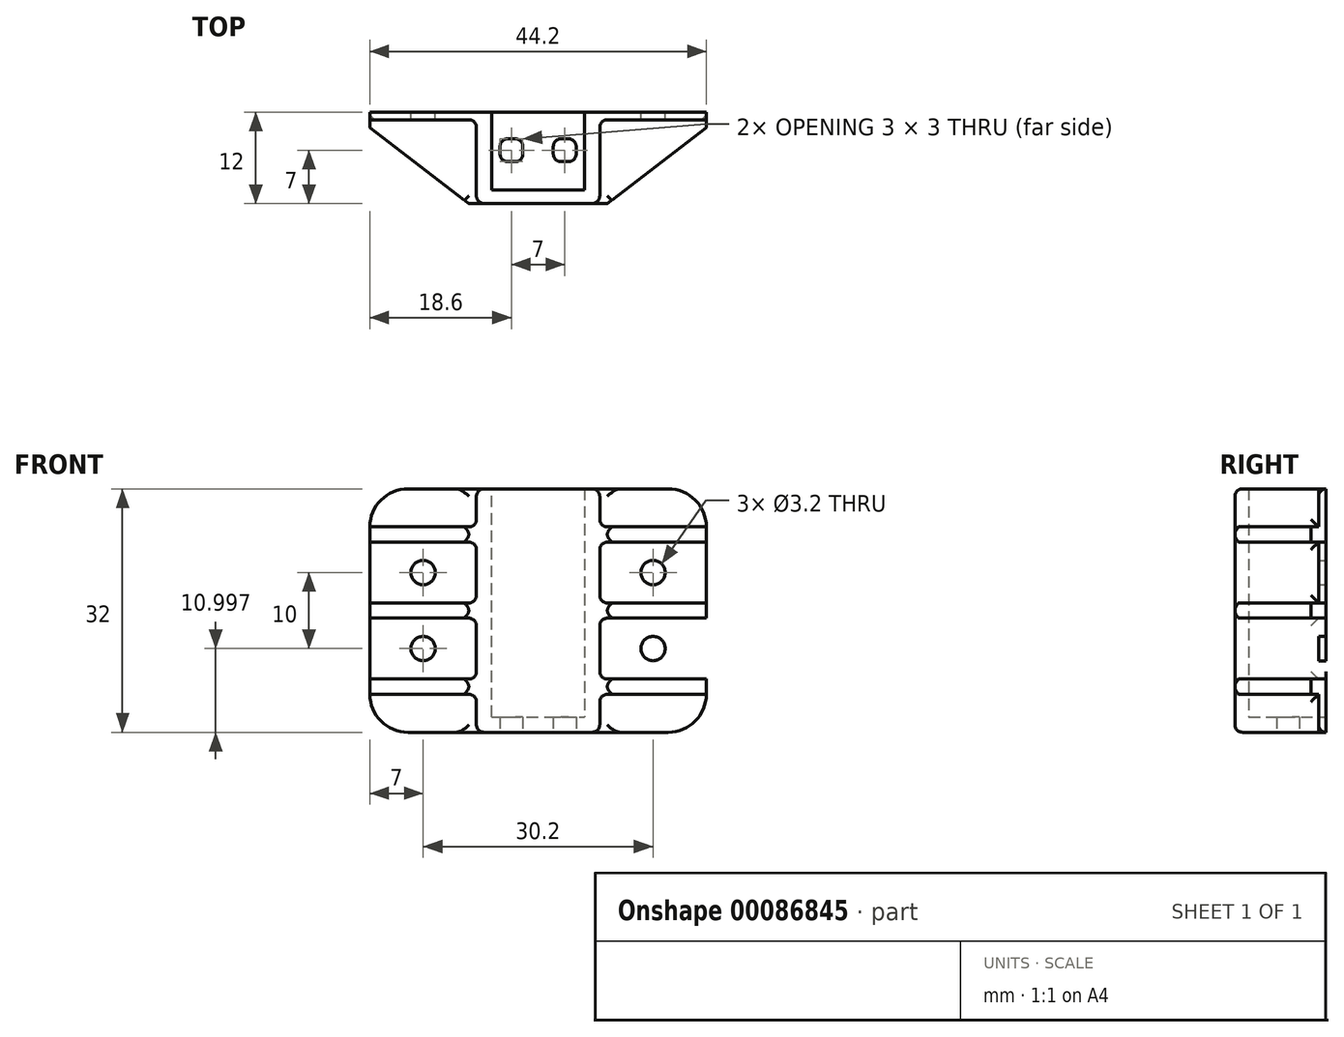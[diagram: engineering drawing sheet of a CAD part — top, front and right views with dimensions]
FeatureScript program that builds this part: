
annotation { "Feature Type Name" : "Feature", "Feature Type Description" : "" }
export const myFeature = defineFeature(function(context is Context, id is Id, definition is map)
    precondition{}
    {
        {
            var Q0;
            Q0=qCreatedBy(makeId("Front.planeOp"),FACE);
            var sketch = newSketch(context, id + "F0", { "sketchPlane" : qUnion([Q0])});
            skLineSegment(sketch, "E0.bottom", {"start": v(-6.1, 29.45) * mm, "end": v(6.1, 29.45) * mm});
            skLineSegment(sketch, "E0.top", {"start": v(-6.1, -0.55) * mm, "end": v(6.1, -0.55) * mm});
            skLineSegment(sketch, "E0.left", {"start": v(-6.1, 29.45) * mm, "end": v(-6.1, -0.55) * mm});
            skLineSegment(sketch, "E0.right", {"start": v(6.1, 29.45) * mm, "end": v(6.1, -0.55) * mm});
            skLineSegment(sketch, "E1.bottom", {"start": v(-22.1, 29.45) * mm, "end": v(22.1, 29.45) * mm});
            skLineSegment(sketch, "E1.top", {"start": v(-22.1, -2.55) * mm, "end": v(22.1, -2.55) * mm});
            skLineSegment(sketch, "E1.left", {"start": v(-22.1, 29.45) * mm, "end": v(-22.1, -2.55) * mm});
            skLineSegment(sketch, "E1.right", {"start": v(22.1, 29.45) * mm, "end": v(22.1, -2.55) * mm});
            skLineSegment(sketch, "E2.bottom", {"start": v(-8.1, 29.45) * mm, "end": v(8.1, 29.45) * mm});
            skLineSegment(sketch, "E2.top", {"start": v(-8.1, -2.55) * mm, "end": v(8.1, -2.55) * mm});
            skLineSegment(sketch, "E2.left", {"start": v(-8.1, 29.45) * mm, "end": v(-8.1, -2.55) * mm});
            skLineSegment(sketch, "E2.right", {"start": v(8.1, 29.45) * mm, "end": v(8.1, -2.55) * mm});
            skLineSegment(sketch, "E3.bottom", {"start": v(-8.1, 24.45) * mm, "end": v(-22.1, 24.45) * mm});
            skLineSegment(sketch, "E3.top", {"start": v(-8.1, 22.45) * mm, "end": v(-22.1, 22.45) * mm});
            skLineSegment(sketch, "E3.left", {"start": v(-8.1, 24.45) * mm, "end": v(-8.1, 22.45) * mm});
            skLineSegment(sketch, "E3.right", {"start": v(-22.1, 24.45) * mm, "end": v(-22.1, 22.45) * mm});
            skLineSegment(sketch, "E4.bottom", {"start": v(-8.1, 14.45) * mm, "end": v(-22.1, 14.45) * mm});
            skLineSegment(sketch, "E4.top", {"start": v(-8.1, 12.45) * mm, "end": v(-22.1, 12.45) * mm});
            skLineSegment(sketch, "E4.left", {"start": v(-8.1, 14.45) * mm, "end": v(-8.1, 12.45) * mm});
            skLineSegment(sketch, "E4.right", {"start": v(-22.1, 14.45) * mm, "end": v(-22.1, 12.45) * mm});
            skLineSegment(sketch, "E5.bottom", {"start": v(-8.1, 4.45) * mm, "end": v(-22.1, 4.45) * mm});
            skLineSegment(sketch, "E5.top", {"start": v(-8.1, 2.45) * mm, "end": v(-22.1, 2.45) * mm});
            skLineSegment(sketch, "E5.left", {"start": v(-8.1, 4.45) * mm, "end": v(-8.1, 2.45) * mm});
            skLineSegment(sketch, "E5.right", {"start": v(-22.1, 4.45) * mm, "end": v(-22.1, 2.45) * mm});
            skPoint(sketch, "E6", {"position": v(-15.1, 18.45) * mm});
            skPoint(sketch, "E6.positionSnap0", {"position": v(-15.1, 22.45) * mm});
            skPoint(sketch, "E7", {"position": v(-15.1, 8.45) * mm});
            skCircle(sketch, "E8", {"center": v(-15.1, 18.45) * mm, "radius": 1.6 * mm});
            skCircle(sketch, "E9", {"center": v(-15.1, 8.45) * mm, "radius": 1.6 * mm});
            skLineSegment(sketch, "E10.MirrorCS", {"start": v(22.1, 24.45) * mm, "end": v(22.1, 22.45) * mm});
            skLineSegment(sketch, "E11.MirrorCS", {"start": v(8.1, 14.45) * mm, "end": v(8.1, 12.45) * mm});
            skLineSegment(sketch, "E12.MirrorCS", {"start": v(8.1, 4.45) * mm, "end": v(8.1, 2.45) * mm});
            skLineSegment(sketch, "E13.MirrorCS", {"start": v(22.1, 4.45) * mm, "end": v(22.1, 2.45) * mm});
            skLineSegment(sketch, "E14.MirrorCS", {"start": v(22.1, 14.45) * mm, "end": v(22.1, 12.45) * mm});
            skLineSegment(sketch, "E15.MirrorCS", {"start": v(8.1, 24.45) * mm, "end": v(8.1, 22.45) * mm});
            skLineSegment(sketch, "E16.MirrorCS", {"start": v(8.1, 14.45) * mm, "end": v(22.1, 14.45) * mm});
            skCircle(sketch, "E17.MirrorC", {"center": v(15.1, 8.45) * mm, "radius": 1.6 * mm});
            skLineSegment(sketch, "E18.MirrorCS", {"start": v(8.1, 4.45) * mm, "end": v(22.1, 4.45) * mm});
            skPoint(sketch, "E19.MirrorP", {"position": v(15.1, 18.45) * mm});
            skLineSegment(sketch, "E20.MirrorCS", {"start": v(8.1, 12.45) * mm, "end": v(22.1, 12.45) * mm});
            skLineSegment(sketch, "E21.MirrorCS", {"start": v(8.1, 22.45) * mm, "end": v(22.1, 22.45) * mm});
            skLineSegment(sketch, "E22.MirrorCS", {"start": v(8.1, 24.45) * mm, "end": v(22.1, 24.45) * mm});
            skLineSegment(sketch, "E23.MirrorCS", {"start": v(8.1, 2.45) * mm, "end": v(22.1, 2.45) * mm});
            skCircle(sketch, "E24.MirrorC", {"center": v(15.1, 18.45) * mm, "radius": 1.6 * mm});
            skPoint(sketch, "E25.MirrorP", {"position": v(15.1, 22.45) * mm});
            skSolve(sketch);
        }
        {
            var Q0;
            {var subQ1=sQuery(id+"F0.wireOp",EDGE,"E1.left");Q0=makeQuery(id+"F0.imprint","IMPRINT",FACE,{"disambiguationData":[TD([[makeQuery(id+"F0.imprint","IMPRINT",EDGE,{"derivedFrom":subQ1}),1.0]])]});}
            var Q1;
            {var subQ2=sQuery(id+"F0.wireOp",EDGE,"E3.bottom");Q1=makeQuery(id+"F0.imprint","IMPRINT",FACE,{"disambiguationData":[TD([[makeQuery(id+"F0.imprint","IMPRINT",EDGE,{"derivedFrom":subQ2}),1.0]])]});}
            var Q2;
            {var subQ2=sQuery(id+"F0.wireOp",EDGE,"E4.bottom");Q2=makeQuery(id+"F0.imprint","IMPRINT",FACE,{"disambiguationData":[TD([[makeQuery(id+"F0.imprint","IMPRINT",EDGE,{"derivedFrom":subQ2}),1.0]])]});}
            var Q3;
            {var subQ0=sQuery(id+"F0.wireOp",EDGE,"E5.bottom");Q3=makeQuery(id+"F0.imprint","IMPRINT",FACE,{"disambiguationData":[TD([[makeQuery(id+"F0.imprint","IMPRINT",EDGE,{"derivedFrom":subQ0}),1.0]])]});}
            var Q4;
            Q4=makeQuery(id+"F0.imprint","IMPRINT",FACE,{"disambiguationData":[TD([[makeQuery(id+"F0.imprint","IMPRINT",EDGE,{"derivedFrom":sQuery(id+"F0.wireOp",EDGE,"E0.top")}),-1.0]])]});
            var Q5;
            {var subQ7=sQuery(id+"F0.wireOp",EDGE,"E1.right");Q5=makeQuery(id+"F0.imprint","IMPRINT",FACE,{"disambiguationData":[TD([[makeQuery(id+"F0.imprint","IMPRINT",EDGE,{"derivedFrom":subQ7}),-1.0]])]});}
            var Q6;
            Q6=makeQuery(id+"F0.imprint","IMPRINT",FACE,{"disambiguationData":[TD([[makeQuery(id+"F0.imprint","IMPRINT",EDGE,{"derivedFrom":sQuery(id+"F0.wireOp",EDGE,"E13.MirrorCS")}),-1.0]])]});
            var Q7;
            Q7=makeQuery(id+"F0.imprint","IMPRINT",FACE,{"disambiguationData":[TD([[makeQuery(id+"F0.imprint","IMPRINT",EDGE,{"derivedFrom":sQuery(id+"F0.wireOp",EDGE,"E14.MirrorCS")}),-1.0]])]});
            var Q8;
            Q8=makeQuery(id+"F0.imprint","IMPRINT",FACE,{"disambiguationData":[TD([[makeQuery(id+"F0.imprint","IMPRINT",EDGE,{"derivedFrom":sQuery(id+"F0.wireOp",EDGE,"E10.MirrorCS")}),-1.0]])]});
            var Q9;
            {var subQ1=sQuery(id+"F0.wireOp",EDGE,"E16.MirrorCS");Q9=makeQuery(id+"F0.imprint","IMPRINT",FACE,{"disambiguationData":[TD([[makeQuery(id+"F0.imprint","IMPRINT",EDGE,{"derivedFrom":subQ1}),1.0]])]});}
            var Q10;
            Q10=makeQuery(id+"F0.imprint","IMPRINT",FACE,{"disambiguationData":[TD([[makeQuery(id+"F0.imprint","IMPRINT",EDGE,{"derivedFrom":sQuery(id+"F0.wireOp",EDGE,"E17.MirrorC")}),1.0]])]});
            var Q11;
            {var subQ1=sQuery(id+"F0.wireOp",EDGE,"E4.top");Q11=makeQuery(id+"F0.imprint","IMPRINT",FACE,{"disambiguationData":[TD([[makeQuery(id+"F0.imprint","IMPRINT",EDGE,{"derivedFrom":subQ1}),1.0]])]});}
            var Q12;
            {var subQ0=sQuery(id+"F0.wireOp",EDGE,"E3.top");Q12=makeQuery(id+"F0.imprint","IMPRINT",FACE,{"disambiguationData":[TD([[makeQuery(id+"F0.imprint","IMPRINT",EDGE,{"derivedFrom":subQ0}),1.0]])]});}
            extrude(context, id + "F1", {"entities" : qUnion([Q0, Q1, Q2, Q3, Q4, Q5, Q6, Q7, Q8, Q9, Q10, Q11, Q12]), "depth" : 1 * mm, "offsetDistance" : 25 * mm});
        }
        {
            var Q0;
            {var subQ2=sQuery(id+"F0.wireOp",EDGE,"E3.bottom");Q0=makeQuery(id+"F0.imprint","IMPRINT",FACE,{"disambiguationData":[TD([[makeQuery(id+"F0.imprint","IMPRINT",EDGE,{"derivedFrom":subQ2}),1.0]])]});}
            var Q1;
            Q1=makeQuery(id+"F0.imprint","IMPRINT",FACE,{"disambiguationData":[TD([[makeQuery(id+"F0.imprint","IMPRINT",EDGE,{"derivedFrom":sQuery(id+"F0.wireOp",EDGE,"E0.top")}),-1.0]])]});
            var Q2;
            {var subQ2=sQuery(id+"F0.wireOp",EDGE,"E4.bottom");Q2=makeQuery(id+"F0.imprint","IMPRINT",FACE,{"disambiguationData":[TD([[makeQuery(id+"F0.imprint","IMPRINT",EDGE,{"derivedFrom":subQ2}),1.0]])]});}
            var Q3;
            {var subQ0=sQuery(id+"F0.wireOp",EDGE,"E5.bottom");Q3=makeQuery(id+"F0.imprint","IMPRINT",FACE,{"disambiguationData":[TD([[makeQuery(id+"F0.imprint","IMPRINT",EDGE,{"derivedFrom":subQ0}),1.0]])]});}
            var Q4;
            {var subQ0=sQuery(id+"F0.wireOp",EDGE,"E18.MirrorCS");Q4=makeQuery(id+"F0.imprint","IMPRINT",FACE,{"disambiguationData":[TD([[makeQuery(id+"F0.imprint","IMPRINT",EDGE,{"derivedFrom":subQ0}),-1.0]])]});}
            var Q5;
            {var subQ2=sQuery(id+"F0.wireOp",EDGE,"E16.MirrorCS");Q5=makeQuery(id+"F0.imprint","IMPRINT",FACE,{"disambiguationData":[TD([[makeQuery(id+"F0.imprint","IMPRINT",EDGE,{"derivedFrom":subQ2}),-1.0]])]});}
            var Q6;
            {var subQ0=sQuery(id+"F0.wireOp",EDGE,"E21.MirrorCS");Q6=makeQuery(id+"F0.imprint","IMPRINT",FACE,{"disambiguationData":[TD([[makeQuery(id+"F0.imprint","IMPRINT",EDGE,{"derivedFrom":subQ0}),1.0]])]});}
            extrude(context, id + "F2", {"entities" : qUnion([Q0, Q1, Q2, Q3, Q4, Q5, Q6]), "operationType" : NewBodyOperationType.ADD, "depth" : 12 * mm, "offsetDistance" : 25 * mm});
        }
        {
            var Q0;
            {var subQ0=sQuery(id+"F0.wireOp",EDGE,"E0.right");Q0=makeQuery(id+"F2.boolean.opBoolean","MERGE",FACE,{"derivedFrom":[makeQuery(id+"F1.opExtrude","SWEPT_FACE",FACE,{"disambiguationData":[OSD([subQ0])]}),makeQuery(id+"F2.opExtrude","SWEPT_FACE",FACE,{"disambiguationData":[OSD([subQ0])]})]});}
            var sketch = newSketch(context, id + "F3", { "sketchPlane" : qUnion([Q0])});
            skLineSegment(sketch, "E26.bottom", {"start": v(12, 29.45) * mm, "end": v(10.2, 29.45) * mm});
            skLineSegment(sketch, "E26.top", {"start": v(12, -0.55) * mm, "end": v(10.2, -0.55) * mm});
            skLineSegment(sketch, "E26.left", {"start": v(12, 29.45) * mm, "end": v(12, -0.55) * mm});
            skLineSegment(sketch, "E26.right", {"start": v(10.2, 29.45) * mm, "end": v(10.2, -0.55) * mm});
            skSolve(sketch);
        }
        {
            var Q0;
            Q0=makeQuery(id+"F3.imprint","IMPRINT",FACE,{"disambiguationData":[TD([[makeQuery(id+"F3.imprint","IMPRINT",EDGE,{"derivedFrom":sQuery(id+"F3.wireOp",EDGE,"E26.bottom")}),1.0]])]});
            extrude(context, id + "F4", {"entities" : qUnion([Q0]), "operationType" : NewBodyOperationType.ADD, "endBound" : BoundingType.UP_TO_NEXT, "depth" : 25 * mm, "offsetDistance" : 25 * mm});
        }
        {
            var Q0;
            Q0=makeQuery(id+"F1.opExtrude","SWEPT_EDGE",EDGE,{"disambiguationData":[OSD([sQuery(id+"F0.wireOp",EDGE,"E1.top"),sQuery(id+"F0.wireOp",EDGE,"E1.right")])]});
            var Q1;
            Q1=makeQuery(id+"F1.opExtrude","SWEPT_EDGE",EDGE,{"disambiguationData":[OSD([sQuery(id+"F0.wireOp",EDGE,"E1.bottom"),sQuery(id+"F0.wireOp",EDGE,"E1.right")])]});
            var Q2;
            Q2=makeQuery(id+"F1.opExtrude","SWEPT_EDGE",EDGE,{"disambiguationData":[OSD([sQuery(id+"F0.wireOp",EDGE,"E1.bottom"),sQuery(id+"F0.wireOp",EDGE,"E1.left")])]});
            var Q3;
            Q3=makeQuery(id+"F1.opExtrude","SWEPT_EDGE",EDGE,{"disambiguationData":[OSD([sQuery(id+"F0.wireOp",EDGE,"E1.top"),sQuery(id+"F0.wireOp",EDGE,"E1.left")])]});
            fillet(context, id + "F5", {"entities" : qUnion([Q0, Q1, Q2, Q3]), "tangentPropagation" : true, "radius" : 5 * mm, "defaultsChanged" : false, "vertexSettings" : [], "allowEdgeOverflow" : false});
        }
        {
            var Q0;
            {var subQ0=sQuery(id+"F0.wireOp",EDGE,"E1.top");Q0=makeQuery(id+"F2.boolean.opBoolean","MERGE",FACE,{"derivedFrom":[makeQuery(id+"F1.opExtrude","SWEPT_FACE",FACE,{"disambiguationData":[OSD([subQ0])]}),makeQuery(id+"F2.opExtrude","SWEPT_FACE",FACE,{"disambiguationData":[OSD([subQ0])]})]});}
            var sketch = newSketch(context, id + "F6", { "sketchPlane" : qUnion([Q0])});
            skPoint(sketch, "E27", {"position": v(0, 0) * mm});
            skLineSegment(sketch, "E28.bottom", {"start": v(2, 3.5) * mm, "end": v(5, 3.5) * mm});
            skLineSegment(sketch, "E28.top", {"start": v(2, 6.5) * mm, "end": v(5, 6.5) * mm});
            skLineSegment(sketch, "E28.left", {"start": v(2, 3.5) * mm, "end": v(2, 6.5) * mm});
            skLineSegment(sketch, "E28.right", {"start": v(5, 3.5) * mm, "end": v(5, 6.5) * mm});
            skLineSegment(sketch, "E29", {"start": v(0, 0) * mm, "end": v(0, 7.3) * mm, "construction": true});
            skLineSegment(sketch, "E30.MirrorCS", {"start": v(-2, 3.5) * mm, "end": v(-2, 6.5) * mm});
            skLineSegment(sketch, "E31.MirrorCS", {"start": v(-5, 3.5) * mm, "end": v(-5, 6.5) * mm});
            skLineSegment(sketch, "E32.MirrorCS", {"start": v(-2, 3.5) * mm, "end": v(-5, 3.5) * mm});
            skLineSegment(sketch, "E33.MirrorCS", {"start": v(-2, 6.5) * mm, "end": v(-5, 6.5) * mm});
            skSolve(sketch);
        }
        {
            var Q0;
            Q0=makeQuery(id+"F6.imprint","IMPRINT",FACE,{"disambiguationData":[TD([[makeQuery(id+"F6.imprint","IMPRINT",EDGE,{"derivedFrom":sQuery(id+"F6.wireOp",EDGE,"E30.MirrorCS")}),1.0]])]});
            var Q1;
            Q1=makeQuery(id+"F6.imprint","IMPRINT",FACE,{"disambiguationData":[TD([[makeQuery(id+"F6.imprint","IMPRINT",EDGE,{"derivedFrom":sQuery(id+"F6.wireOp",EDGE,"E28.bottom")}),1.0]])]});
            extrude(context, id + "F7", {"entities" : qUnion([Q0, Q1]), "operationType" : NewBodyOperationType.REMOVE, "oppositeDirection" : true, "depth" : 25 * mm, "offsetDistance" : 25 * mm});
        }
        {
            var Q0;
            {var subQ0=sQuery(id+"F0.wireOp",EDGE,"E1.left");Q0=makeQuery(id+"F2.opExtrude","CAP_EDGE",EDGE,{"disambiguationData":[OSD([subQ0]),TDD([makeQuery(id+"F0.imprint","IMPRINT",EDGE,{"disambiguationData":[TD([[makeQuery(id+"F0.imprint","INTERSECT",VERTEX,{"derivedFrom":[subQ0,sQuery(id+"F0.wireOp",EDGE,"E3.top")]}),1.0]])],"derivedFrom":subQ0})])],"isStart":false});}
            var Q1;
            {var subQ0=sQuery(id+"F0.wireOp",EDGE,"E1.left");Q1=makeQuery(id+"F2.opExtrude","CAP_EDGE",EDGE,{"disambiguationData":[OSD([subQ0]),TDD([makeQuery(id+"F0.imprint","IMPRINT",EDGE,{"disambiguationData":[TD([[makeQuery(id+"F0.imprint","INTERSECT",VERTEX,{"derivedFrom":[subQ0,sQuery(id+"F0.wireOp",EDGE,"E4.top")]}),1.0]])],"derivedFrom":subQ0})])],"isStart":false});}
            var Q2;
            {var subQ0=sQuery(id+"F0.wireOp",EDGE,"E1.left");Q2=makeQuery(id+"F2.opExtrude","CAP_EDGE",EDGE,{"disambiguationData":[OSD([subQ0]),TDD([makeQuery(id+"F0.imprint","IMPRINT",EDGE,{"disambiguationData":[TD([[makeQuery(id+"F0.imprint","INTERSECT",VERTEX,{"derivedFrom":[subQ0,sQuery(id+"F0.wireOp",EDGE,"E5.bottom")]}),-1.0]])],"derivedFrom":subQ0})])],"isStart":false});}
            chamfer(context, id + "F8", {"entities" : qUnion([Q0, Q1, Q2]), "chamferType" : ChamferType.TWO_OFFSETS, "width1" : 13 * mm, "oppositeDirection" : false, "width2" : 10 * mm, "tangentPropagation" : true});
        }
        {
            var Q0;
            {var subQ0=sQuery(id+"F0.wireOp",EDGE,"E1.right");Q0=makeQuery(id+"F2.opExtrude","CAP_EDGE",EDGE,{"disambiguationData":[OSD([subQ0]),TDD([makeQuery(id+"F0.imprint","IMPRINT",EDGE,{"disambiguationData":[TD([[makeQuery(id+"F0.imprint","INTERSECT",VERTEX,{"derivedFrom":[subQ0,sQuery(id+"F0.wireOp",EDGE,"E18.MirrorCS")]}),-1.0]])],"derivedFrom":subQ0})])],"isStart":false});}
            var Q1;
            {var subQ0=sQuery(id+"F0.wireOp",EDGE,"E1.right");Q1=makeQuery(id+"F2.opExtrude","CAP_EDGE",EDGE,{"disambiguationData":[OSD([subQ0]),TDD([makeQuery(id+"F0.imprint","IMPRINT",EDGE,{"disambiguationData":[TD([[makeQuery(id+"F0.imprint","INTERSECT",VERTEX,{"derivedFrom":[subQ0,sQuery(id+"F0.wireOp",EDGE,"E20.MirrorCS")]}),1.0]])],"derivedFrom":subQ0})])],"isStart":false});}
            var Q2;
            {var subQ0=sQuery(id+"F0.wireOp",EDGE,"E1.right");Q2=makeQuery(id+"F2.opExtrude","CAP_EDGE",EDGE,{"disambiguationData":[OSD([subQ0]),TDD([makeQuery(id+"F0.imprint","IMPRINT",EDGE,{"disambiguationData":[TD([[makeQuery(id+"F0.imprint","INTERSECT",VERTEX,{"derivedFrom":[subQ0,sQuery(id+"F0.wireOp",EDGE,"E21.MirrorCS")]}),1.0]])],"derivedFrom":subQ0})])],"isStart":false});}
            chamfer(context, id + "F9", {"entities" : qUnion([Q0, Q1, Q2]), "chamferType" : ChamferType.TWO_OFFSETS, "width1" : 10 * mm, "oppositeDirection" : false, "width2" : 13 * mm, "tangentPropagation" : true});
        }
        {
            var Q0;
            Q0=makeQuery(id+"F2.opExtrude","SWEPT_EDGE",EDGE,{"disambiguationData":[OSD([sQuery(id+"F0.wireOp",EDGE,"E2.right"),sQuery(id+"F0.wireOp",EDGE,"E22.MirrorCS")])]});
            var Q1;
            Q1=makeQuery(id+"F2.opExtrude","SWEPT_EDGE",EDGE,{"disambiguationData":[OSD([sQuery(id+"F0.wireOp",EDGE,"E2.right"),sQuery(id+"F0.wireOp",EDGE,"E21.MirrorCS")])]});
            var Q2;
            Q2=makeQuery(id+"F2.opExtrude","SWEPT_EDGE",EDGE,{"disambiguationData":[OSD([sQuery(id+"F0.wireOp",EDGE,"E2.right"),sQuery(id+"F0.wireOp",EDGE,"E16.MirrorCS")])]});
            var Q3;
            Q3=makeQuery(id+"F2.opExtrude","SWEPT_EDGE",EDGE,{"disambiguationData":[OSD([sQuery(id+"F0.wireOp",EDGE,"E2.right"),sQuery(id+"F0.wireOp",EDGE,"E20.MirrorCS")])]});
            var Q4;
            Q4=makeQuery(id+"F2.opExtrude","SWEPT_EDGE",EDGE,{"disambiguationData":[OSD([sQuery(id+"F0.wireOp",EDGE,"E2.right"),sQuery(id+"F0.wireOp",EDGE,"E18.MirrorCS")])]});
            var Q5;
            Q5=makeQuery(id+"F2.opExtrude","SWEPT_EDGE",EDGE,{"disambiguationData":[OSD([sQuery(id+"F0.wireOp",EDGE,"E2.right"),sQuery(id+"F0.wireOp",EDGE,"E23.MirrorCS")])]});
            var Q6;
            Q6=makeQuery(id+"F2.opExtrude","SWEPT_EDGE",EDGE,{"disambiguationData":[OSD([sQuery(id+"F0.wireOp",EDGE,"E2.left"),sQuery(id+"F0.wireOp",EDGE,"E3.bottom")])]});
            var Q7;
            Q7=makeQuery(id+"F2.opExtrude","SWEPT_EDGE",EDGE,{"disambiguationData":[OSD([sQuery(id+"F0.wireOp",EDGE,"E2.left"),sQuery(id+"F0.wireOp",EDGE,"E4.bottom")])]});
            var Q8;
            Q8=makeQuery(id+"F2.opExtrude","SWEPT_EDGE",EDGE,{"disambiguationData":[OSD([sQuery(id+"F0.wireOp",EDGE,"E2.left"),sQuery(id+"F0.wireOp",EDGE,"E5.bottom")])]});
            var Q9;
            Q9=makeQuery(id+"F2.opExtrude","SWEPT_EDGE",EDGE,{"disambiguationData":[OSD([sQuery(id+"F0.wireOp",EDGE,"E2.left"),sQuery(id+"F0.wireOp",EDGE,"E5.top")])]});
            var Q10;
            Q10=makeQuery(id+"F2.opExtrude","SWEPT_EDGE",EDGE,{"disambiguationData":[OSD([sQuery(id+"F0.wireOp",EDGE,"E2.left"),sQuery(id+"F0.wireOp",EDGE,"E4.top")])]});
            var Q11;
            Q11=makeQuery(id+"F2.opExtrude","SWEPT_EDGE",EDGE,{"disambiguationData":[OSD([sQuery(id+"F0.wireOp",EDGE,"E2.left"),sQuery(id+"F0.wireOp",EDGE,"E3.top")])]});
            var Q12;
            Q12=makeQuery(id+"F2.opExtrude","SWEPT_EDGE",EDGE,{"disambiguationData":[OSD([sQuery(id+"F0.wireOp",EDGE,"E1.bottom"),sQuery(id+"F0.wireOp",EDGE,"E2.left")])]});
            var Q13;
            Q13=makeQuery(id+"F2.opExtrude","SWEPT_EDGE",EDGE,{"disambiguationData":[OSD([sQuery(id+"F0.wireOp",EDGE,"E1.bottom"),sQuery(id+"F0.wireOp",EDGE,"E2.right")])]});
            var Q14;
            {var subQ0=sQuery(id+"F0.wireOp",EDGE,"E1.bottom");var subQ1=sQuery(id+"F0.wireOp",EDGE,"E0.right");var subQ2=sQuery(id+"F0.wireOp",EDGE,"E0.bottom");Q14=makeQuery(id+"F4.boolean.opBoolean","MERGE",EDGE,{"derivedFrom":[makeQuery(id+"F2.opExtrude","CAP_EDGE",EDGE,{"disambiguationData":[OSD([subQ0]),TDD([makeQuery(id+"F0.imprint","IMPRINT",EDGE,{"disambiguationData":[TD([[makeQuery(id+"F0.imprint","INTERSECT",VERTEX,{"derivedFrom":[subQ0,sQuery(id+"F0.wireOp",EDGE,"E2.right")]}),1.0]])],"derivedFrom":subQ0})])],"isStart":false}),makeQuery(id+"F2.opExtrude","CAP_EDGE",EDGE,{"disambiguationData":[OSD([subQ0]),TDD([makeQuery(id+"F0.imprint","IMPRINT",EDGE,{"disambiguationData":[TD([[makeQuery(id+"F0.imprint","INTERSECT",VERTEX,{"derivedFrom":[subQ0,sQuery(id+"F0.wireOp",EDGE,"E2.left")]}),-1.0]])],"derivedFrom":subQ0})])],"isStart":false}),makeQuery(id+"F4.opExtrude","SWEPT_EDGE",EDGE,{"disambiguationData":[OSD([subQ2,subQ1,subQ0,sQuery(id+"F3.wireOp",EDGE,"E26.bottom"),sQuery(id+"F3.wireOp",EDGE,"E26.left")])]})]});}
            var Q15;
            Q15=makeQuery(id+"F2.opExtrude","SWEPT_EDGE",EDGE,{"disambiguationData":[OSD([sQuery(id+"F0.wireOp",EDGE,"E1.top"),sQuery(id+"F0.wireOp",EDGE,"E2.right")])]});
            var Q16;
            Q16=makeQuery(id+"F2.opExtrude","SWEPT_EDGE",EDGE,{"disambiguationData":[OSD([sQuery(id+"F0.wireOp",EDGE,"E1.top"),sQuery(id+"F0.wireOp",EDGE,"E2.left")])]});
            var Q17;
            Q17=makeQuery(id+"F2.opExtrude","CAP_EDGE",EDGE,{"disambiguationData":[OSD([sQuery(id+"F0.wireOp",EDGE,"E1.top")])],"isStart":false});
            var Q18;
            {var subQ0=sQuery(id+"F0.wireOp",EDGE,"E2.right");Q18=makeQuery(id+"F2.opExtrude","CAP_EDGE",EDGE,{"disambiguationData":[OSD([subQ0]),TDD([makeQuery(id+"F0.imprint","IMPRINT",EDGE,{"disambiguationData":[TD([[makeQuery(id+"F0.imprint","INTERSECT",VERTEX,{"derivedFrom":[sQuery(id+"F0.wireOp",EDGE,"E1.bottom"),subQ0]}),-1.0]])],"derivedFrom":subQ0})])],"isStart":false});}
            var Q19;
            {var subQ0=sQuery(id+"F0.wireOp",EDGE,"E2.left");Q19=makeQuery(id+"F2.opExtrude","CAP_EDGE",EDGE,{"disambiguationData":[OSD([subQ0]),TDD([makeQuery(id+"F0.imprint","IMPRINT",EDGE,{"disambiguationData":[TD([[makeQuery(id+"F0.imprint","INTERSECT",VERTEX,{"derivedFrom":[subQ0,sQuery(id+"F0.wireOp",EDGE,"E3.bottom")]}),1.0]])],"derivedFrom":subQ0})])],"isStart":false});}
            var Q20;
            {var subQ0=sQuery(id+"F0.wireOp",EDGE,"E2.right");Q20=makeQuery(id+"F2.opExtrude","CAP_EDGE",EDGE,{"disambiguationData":[OSD([subQ0]),TDD([makeQuery(id+"F0.imprint","IMPRINT",EDGE,{"disambiguationData":[TD([[makeQuery(id+"F0.imprint","INTERSECT",VERTEX,{"derivedFrom":[subQ0,sQuery(id+"F0.wireOp",EDGE,"E21.MirrorCS")]}),-1.0]])],"derivedFrom":subQ0})])],"isStart":false});}
            var Q21;
            {var subQ0=sQuery(id+"F0.wireOp",EDGE,"E2.right");Q21=makeQuery(id+"F2.opExtrude","CAP_EDGE",EDGE,{"disambiguationData":[OSD([subQ0]),TDD([makeQuery(id+"F0.imprint","IMPRINT",EDGE,{"disambiguationData":[TD([[makeQuery(id+"F0.imprint","INTERSECT",VERTEX,{"derivedFrom":[subQ0,sQuery(id+"F0.wireOp",EDGE,"E20.MirrorCS")]}),-1.0]])],"derivedFrom":subQ0})])],"isStart":false});}
            var Q22;
            {var subQ0=sQuery(id+"F0.wireOp",EDGE,"E2.right");Q22=makeQuery(id+"F2.opExtrude","CAP_EDGE",EDGE,{"disambiguationData":[OSD([subQ0]),TDD([makeQuery(id+"F0.imprint","IMPRINT",EDGE,{"disambiguationData":[TD([[makeQuery(id+"F0.imprint","INTERSECT",VERTEX,{"derivedFrom":[subQ0,sQuery(id+"F0.wireOp",EDGE,"E23.MirrorCS")]}),-1.0]])],"derivedFrom":subQ0})])],"isStart":false});}
            var Q23;
            {var subQ0=sQuery(id+"F0.wireOp",EDGE,"E2.left");Q23=makeQuery(id+"F2.opExtrude","CAP_EDGE",EDGE,{"disambiguationData":[OSD([subQ0]),TDD([makeQuery(id+"F0.imprint","IMPRINT",EDGE,{"disambiguationData":[TD([[makeQuery(id+"F0.imprint","INTERSECT",VERTEX,{"derivedFrom":[subQ0,sQuery(id+"F0.wireOp",EDGE,"E3.top")]}),-1.0]])],"derivedFrom":subQ0})])],"isStart":false});}
            var Q24;
            {var subQ0=sQuery(id+"F0.wireOp",EDGE,"E2.left");Q24=makeQuery(id+"F2.opExtrude","CAP_EDGE",EDGE,{"disambiguationData":[OSD([subQ0]),TDD([makeQuery(id+"F0.imprint","IMPRINT",EDGE,{"disambiguationData":[TD([[makeQuery(id+"F0.imprint","INTERSECT",VERTEX,{"derivedFrom":[subQ0,sQuery(id+"F0.wireOp",EDGE,"E4.top")]}),-1.0]])],"derivedFrom":subQ0})])],"isStart":false});}
            var Q25;
            {var subQ0=sQuery(id+"F0.wireOp",EDGE,"E2.left");Q25=makeQuery(id+"F2.opExtrude","CAP_EDGE",EDGE,{"disambiguationData":[OSD([subQ0]),TDD([makeQuery(id+"F0.imprint","IMPRINT",EDGE,{"disambiguationData":[TD([[makeQuery(id+"F0.imprint","INTERSECT",VERTEX,{"derivedFrom":[sQuery(id+"F0.wireOp",EDGE,"E1.top"),subQ0]}),1.0]])],"derivedFrom":subQ0})])],"isStart":false});}
            var Q26;
            {var subQ0=sQuery(id+"F0.wireOp",EDGE,"E2.left");var subQ1=sQuery(id+"F0.wireOp",EDGE,"E1.bottom");Q26=makeQuery(id+"F2.boolean.opBoolean","INTERSECT",EDGE,{"derivedFrom":[makeQuery(id+"F1.opExtrude","CAP_FACE",FACE,{"disambiguationData":[OSD([sQuery(id+"F0.wireOp",EDGE,"E0.top"),sQuery(id+"F0.wireOp",EDGE,"E0.left"),sQuery(id+"F0.wireOp",EDGE,"E0.right"),subQ1,sQuery(id+"F0.wireOp",EDGE,"E1.top"),sQuery(id+"F0.wireOp",EDGE,"E1.left"),sQuery(id+"F0.wireOp",EDGE,"E1.right"),sQuery(id+"F0.wireOp",EDGE,"E8"),sQuery(id+"F0.wireOp",EDGE,"E9"),sQuery(id+"F0.wireOp",EDGE,"E17.MirrorC"),sQuery(id+"F0.wireOp",EDGE,"E24.MirrorC")])],"isStart":false}),makeQuery(id+"F2.opExtrude","SWEPT_FACE",FACE,{"disambiguationData":[OSD([subQ0]),TDD([makeQuery(id+"F0.imprint","IMPRINT",EDGE,{"disambiguationData":[TD([[makeQuery(id+"F0.imprint","INTERSECT",VERTEX,{"derivedFrom":[subQ0,sQuery(id+"F0.wireOp",EDGE,"E3.bottom")]}),1.0]])],"derivedFrom":subQ0})])]})]});}
            var Q27;
            {var subQ0=sQuery(id+"F0.wireOp",EDGE,"E2.left");Q27=makeQuery(id+"F2.boolean.opBoolean","INTERSECT",EDGE,{"derivedFrom":[makeQuery(id+"F1.opExtrude","CAP_FACE",FACE,{"disambiguationData":[OSD([sQuery(id+"F0.wireOp",EDGE,"E0.top"),sQuery(id+"F0.wireOp",EDGE,"E0.left"),sQuery(id+"F0.wireOp",EDGE,"E0.right"),sQuery(id+"F0.wireOp",EDGE,"E1.bottom"),sQuery(id+"F0.wireOp",EDGE,"E1.top"),sQuery(id+"F0.wireOp",EDGE,"E1.left"),sQuery(id+"F0.wireOp",EDGE,"E1.right"),sQuery(id+"F0.wireOp",EDGE,"E8"),sQuery(id+"F0.wireOp",EDGE,"E9"),sQuery(id+"F0.wireOp",EDGE,"E17.MirrorC"),sQuery(id+"F0.wireOp",EDGE,"E24.MirrorC")])],"isStart":false}),makeQuery(id+"F2.opExtrude","SWEPT_FACE",FACE,{"disambiguationData":[OSD([subQ0]),TDD([makeQuery(id+"F0.imprint","IMPRINT",EDGE,{"disambiguationData":[TD([[makeQuery(id+"F0.imprint","INTERSECT",VERTEX,{"derivedFrom":[subQ0,sQuery(id+"F0.wireOp",EDGE,"E3.top")]}),-1.0]])],"derivedFrom":subQ0})])]})]});}
            var Q28;
            {var subQ0=sQuery(id+"F0.wireOp",EDGE,"E2.left");Q28=makeQuery(id+"F2.boolean.opBoolean","INTERSECT",EDGE,{"derivedFrom":[makeQuery(id+"F1.opExtrude","CAP_FACE",FACE,{"disambiguationData":[OSD([sQuery(id+"F0.wireOp",EDGE,"E0.top"),sQuery(id+"F0.wireOp",EDGE,"E0.left"),sQuery(id+"F0.wireOp",EDGE,"E0.right"),sQuery(id+"F0.wireOp",EDGE,"E1.bottom"),sQuery(id+"F0.wireOp",EDGE,"E1.top"),sQuery(id+"F0.wireOp",EDGE,"E1.left"),sQuery(id+"F0.wireOp",EDGE,"E1.right"),sQuery(id+"F0.wireOp",EDGE,"E8"),sQuery(id+"F0.wireOp",EDGE,"E9"),sQuery(id+"F0.wireOp",EDGE,"E17.MirrorC"),sQuery(id+"F0.wireOp",EDGE,"E24.MirrorC")])],"isStart":false}),makeQuery(id+"F2.opExtrude","SWEPT_FACE",FACE,{"disambiguationData":[OSD([subQ0]),TDD([makeQuery(id+"F0.imprint","IMPRINT",EDGE,{"disambiguationData":[TD([[makeQuery(id+"F0.imprint","INTERSECT",VERTEX,{"derivedFrom":[subQ0,sQuery(id+"F0.wireOp",EDGE,"E4.top")]}),-1.0]])],"derivedFrom":subQ0})])]})]});}
            var Q29;
            {var subQ0=sQuery(id+"F0.wireOp",EDGE,"E2.left");var subQ1=sQuery(id+"F0.wireOp",EDGE,"E1.top");Q29=makeQuery(id+"F2.boolean.opBoolean","INTERSECT",EDGE,{"derivedFrom":[makeQuery(id+"F1.opExtrude","CAP_FACE",FACE,{"disambiguationData":[OSD([sQuery(id+"F0.wireOp",EDGE,"E0.top"),sQuery(id+"F0.wireOp",EDGE,"E0.left"),sQuery(id+"F0.wireOp",EDGE,"E0.right"),sQuery(id+"F0.wireOp",EDGE,"E1.bottom"),subQ1,sQuery(id+"F0.wireOp",EDGE,"E1.left"),sQuery(id+"F0.wireOp",EDGE,"E1.right"),sQuery(id+"F0.wireOp",EDGE,"E8"),sQuery(id+"F0.wireOp",EDGE,"E9"),sQuery(id+"F0.wireOp",EDGE,"E17.MirrorC"),sQuery(id+"F0.wireOp",EDGE,"E24.MirrorC")])],"isStart":false}),makeQuery(id+"F2.opExtrude","SWEPT_FACE",FACE,{"disambiguationData":[OSD([subQ0]),TDD([makeQuery(id+"F0.imprint","IMPRINT",EDGE,{"disambiguationData":[TD([[makeQuery(id+"F0.imprint","INTERSECT",VERTEX,{"derivedFrom":[subQ1,subQ0]}),1.0]])],"derivedFrom":subQ0})])]})]});}
            var Q30;
            {var subQ0=sQuery(id+"F0.wireOp",EDGE,"E2.right");var subQ1=sQuery(id+"F0.wireOp",EDGE,"E1.bottom");Q30=makeQuery(id+"F2.boolean.opBoolean","INTERSECT",EDGE,{"derivedFrom":[makeQuery(id+"F1.opExtrude","CAP_FACE",FACE,{"disambiguationData":[OSD([sQuery(id+"F0.wireOp",EDGE,"E0.top"),sQuery(id+"F0.wireOp",EDGE,"E0.left"),sQuery(id+"F0.wireOp",EDGE,"E0.right"),subQ1,sQuery(id+"F0.wireOp",EDGE,"E1.top"),sQuery(id+"F0.wireOp",EDGE,"E1.left"),sQuery(id+"F0.wireOp",EDGE,"E1.right"),sQuery(id+"F0.wireOp",EDGE,"E8"),sQuery(id+"F0.wireOp",EDGE,"E9"),sQuery(id+"F0.wireOp",EDGE,"E17.MirrorC"),sQuery(id+"F0.wireOp",EDGE,"E24.MirrorC")])],"isStart":false}),makeQuery(id+"F2.opExtrude","SWEPT_FACE",FACE,{"disambiguationData":[OSD([subQ0]),TDD([makeQuery(id+"F0.imprint","IMPRINT",EDGE,{"disambiguationData":[TD([[makeQuery(id+"F0.imprint","INTERSECT",VERTEX,{"derivedFrom":[subQ1,subQ0]}),-1.0]])],"derivedFrom":subQ0})])]})]});}
            var Q31;
            {var subQ0=sQuery(id+"F0.wireOp",EDGE,"E2.right");Q31=makeQuery(id+"F2.boolean.opBoolean","INTERSECT",EDGE,{"derivedFrom":[makeQuery(id+"F1.opExtrude","CAP_FACE",FACE,{"disambiguationData":[OSD([sQuery(id+"F0.wireOp",EDGE,"E0.top"),sQuery(id+"F0.wireOp",EDGE,"E0.left"),sQuery(id+"F0.wireOp",EDGE,"E0.right"),sQuery(id+"F0.wireOp",EDGE,"E1.bottom"),sQuery(id+"F0.wireOp",EDGE,"E1.top"),sQuery(id+"F0.wireOp",EDGE,"E1.left"),sQuery(id+"F0.wireOp",EDGE,"E1.right"),sQuery(id+"F0.wireOp",EDGE,"E8"),sQuery(id+"F0.wireOp",EDGE,"E9"),sQuery(id+"F0.wireOp",EDGE,"E17.MirrorC"),sQuery(id+"F0.wireOp",EDGE,"E24.MirrorC")])],"isStart":false}),makeQuery(id+"F2.opExtrude","SWEPT_FACE",FACE,{"disambiguationData":[OSD([subQ0]),TDD([makeQuery(id+"F0.imprint","IMPRINT",EDGE,{"disambiguationData":[TD([[makeQuery(id+"F0.imprint","INTERSECT",VERTEX,{"derivedFrom":[subQ0,sQuery(id+"F0.wireOp",EDGE,"E21.MirrorCS")]}),-1.0]])],"derivedFrom":subQ0})])]})]});}
            var Q32;
            {var subQ0=sQuery(id+"F0.wireOp",EDGE,"E2.right");Q32=makeQuery(id+"F2.boolean.opBoolean","INTERSECT",EDGE,{"derivedFrom":[makeQuery(id+"F1.opExtrude","CAP_FACE",FACE,{"disambiguationData":[OSD([sQuery(id+"F0.wireOp",EDGE,"E0.top"),sQuery(id+"F0.wireOp",EDGE,"E0.left"),sQuery(id+"F0.wireOp",EDGE,"E0.right"),sQuery(id+"F0.wireOp",EDGE,"E1.bottom"),sQuery(id+"F0.wireOp",EDGE,"E1.top"),sQuery(id+"F0.wireOp",EDGE,"E1.left"),sQuery(id+"F0.wireOp",EDGE,"E1.right"),sQuery(id+"F0.wireOp",EDGE,"E8"),sQuery(id+"F0.wireOp",EDGE,"E9"),sQuery(id+"F0.wireOp",EDGE,"E17.MirrorC"),sQuery(id+"F0.wireOp",EDGE,"E24.MirrorC")])],"isStart":false}),makeQuery(id+"F2.opExtrude","SWEPT_FACE",FACE,{"disambiguationData":[OSD([subQ0]),TDD([makeQuery(id+"F0.imprint","IMPRINT",EDGE,{"disambiguationData":[TD([[makeQuery(id+"F0.imprint","INTERSECT",VERTEX,{"derivedFrom":[subQ0,sQuery(id+"F0.wireOp",EDGE,"E20.MirrorCS")]}),-1.0]])],"derivedFrom":subQ0})])]})]});}
            var Q33;
            {var subQ0=sQuery(id+"F0.wireOp",EDGE,"E2.right");var subQ1=sQuery(id+"F0.wireOp",EDGE,"E1.top");Q33=makeQuery(id+"F2.boolean.opBoolean","INTERSECT",EDGE,{"derivedFrom":[makeQuery(id+"F1.opExtrude","CAP_FACE",FACE,{"disambiguationData":[OSD([sQuery(id+"F0.wireOp",EDGE,"E0.top"),sQuery(id+"F0.wireOp",EDGE,"E0.left"),sQuery(id+"F0.wireOp",EDGE,"E0.right"),sQuery(id+"F0.wireOp",EDGE,"E1.bottom"),subQ1,sQuery(id+"F0.wireOp",EDGE,"E1.left"),sQuery(id+"F0.wireOp",EDGE,"E1.right"),sQuery(id+"F0.wireOp",EDGE,"E8"),sQuery(id+"F0.wireOp",EDGE,"E9"),sQuery(id+"F0.wireOp",EDGE,"E17.MirrorC"),sQuery(id+"F0.wireOp",EDGE,"E24.MirrorC")])],"isStart":false}),makeQuery(id+"F2.opExtrude","SWEPT_FACE",FACE,{"disambiguationData":[OSD([subQ0]),TDD([makeQuery(id+"F0.imprint","IMPRINT",EDGE,{"disambiguationData":[TD([[makeQuery(id+"F0.imprint","INTERSECT",VERTEX,{"derivedFrom":[subQ0,sQuery(id+"F0.wireOp",EDGE,"E23.MirrorCS")]}),-1.0]])],"derivedFrom":subQ0})])]})]});}
            var Q34;
            {var subQ0=sQuery(id+"F0.wireOp",EDGE,"E1.right");var subQ1=sQuery(id+"F0.wireOp",EDGE,"E16.MirrorCS");Q34=makeQuery(id+"F2.boolean.opBoolean","SPLIT",EDGE,{"disambiguationData":[TD([makeQuery(id+"F2.opExtrude","SWEPT_FACE",FACE,{"disambiguationData":[OSD([subQ1])]})])],"derivedFrom":makeQuery(id+"F1.opExtrude","CAP_EDGE",EDGE,{"disambiguationData":[OSD([subQ0])],"isStart":false})});}
            var Q35;
            {var subQ1=sQuery(id+"F0.wireOp",EDGE,"E1.right");var subQ2=sQuery(id+"F0.wireOp",EDGE,"E18.MirrorCS");Q35=makeQuery(id+"F2.boolean.opBoolean","SPLIT",EDGE,{"disambiguationData":[TD([makeQuery(id+"F2.opExtrude","SWEPT_FACE",FACE,{"disambiguationData":[OSD([subQ2])]})])],"derivedFrom":makeQuery(id+"F1.opExtrude","CAP_EDGE",EDGE,{"disambiguationData":[OSD([subQ1])],"isStart":false})});}
            var Q36;
            {var subQ0=sQuery(id+"F0.wireOp",EDGE,"E1.left");var subQ2=sQuery(id+"F0.wireOp",EDGE,"E3.top");Q36=makeQuery(id+"F2.boolean.opBoolean","SPLIT",EDGE,{"disambiguationData":[TD([makeQuery(id+"F2.opExtrude","SWEPT_FACE",FACE,{"disambiguationData":[OSD([subQ2])]})])],"derivedFrom":makeQuery(id+"F1.opExtrude","CAP_EDGE",EDGE,{"disambiguationData":[OSD([subQ0])],"isStart":false})});}
            var Q37;
            {var subQ1=sQuery(id+"F0.wireOp",EDGE,"E1.left");var subQ2=sQuery(id+"F0.wireOp",EDGE,"E4.top");Q37=makeQuery(id+"F2.boolean.opBoolean","SPLIT",EDGE,{"disambiguationData":[TD([makeQuery(id+"F2.opExtrude","SWEPT_FACE",FACE,{"disambiguationData":[OSD([subQ2])]})])],"derivedFrom":makeQuery(id+"F1.opExtrude","CAP_EDGE",EDGE,{"disambiguationData":[OSD([subQ1])],"isStart":false})});}
            var Q38;
            Q38=makeQuery(id+"F7.boolean.opBoolean","COPY",EDGE,{"derivedFrom":makeQuery(id+"F7.opExtrude","SWEPT_EDGE",EDGE,{"disambiguationData":[OSD([sQuery(id+"F6.wireOp",EDGE,"E31.MirrorCS"),sQuery(id+"F6.wireOp",EDGE,"E33.MirrorCS")])]})});
            var Q39;
            Q39=makeQuery(id+"F7.boolean.opBoolean","COPY",EDGE,{"derivedFrom":makeQuery(id+"F7.opExtrude","SWEPT_EDGE",EDGE,{"disambiguationData":[OSD([sQuery(id+"F6.wireOp",EDGE,"E30.MirrorCS"),sQuery(id+"F6.wireOp",EDGE,"E33.MirrorCS")])]})});
            var Q40;
            Q40=makeQuery(id+"F7.boolean.opBoolean","COPY",EDGE,{"derivedFrom":makeQuery(id+"F7.opExtrude","SWEPT_EDGE",EDGE,{"disambiguationData":[OSD([sQuery(id+"F6.wireOp",EDGE,"E28.top"),sQuery(id+"F6.wireOp",EDGE,"E28.left")])]})});
            var Q41;
            Q41=makeQuery(id+"F7.boolean.opBoolean","COPY",EDGE,{"derivedFrom":makeQuery(id+"F7.opExtrude","SWEPT_EDGE",EDGE,{"disambiguationData":[OSD([sQuery(id+"F6.wireOp",EDGE,"E28.top"),sQuery(id+"F6.wireOp",EDGE,"E28.right")])]})});
            var Q42;
            Q42=makeQuery(id+"F7.boolean.opBoolean","COPY",EDGE,{"derivedFrom":makeQuery(id+"F7.opExtrude","SWEPT_EDGE",EDGE,{"disambiguationData":[OSD([sQuery(id+"F6.wireOp",EDGE,"E31.MirrorCS"),sQuery(id+"F6.wireOp",EDGE,"E32.MirrorCS")])]})});
            var Q43;
            Q43=makeQuery(id+"F7.boolean.opBoolean","COPY",EDGE,{"derivedFrom":makeQuery(id+"F7.opExtrude","SWEPT_EDGE",EDGE,{"disambiguationData":[OSD([sQuery(id+"F6.wireOp",EDGE,"E28.bottom"),sQuery(id+"F6.wireOp",EDGE,"E28.left")])]})});
            var Q44;
            Q44=makeQuery(id+"F7.boolean.opBoolean","COPY",EDGE,{"derivedFrom":makeQuery(id+"F7.opExtrude","SWEPT_EDGE",EDGE,{"disambiguationData":[OSD([sQuery(id+"F6.wireOp",EDGE,"E30.MirrorCS"),sQuery(id+"F6.wireOp",EDGE,"E32.MirrorCS")])]})});
            var Q45;
            Q45=makeQuery(id+"F7.boolean.opBoolean","COPY",EDGE,{"derivedFrom":makeQuery(id+"F7.opExtrude","SWEPT_EDGE",EDGE,{"disambiguationData":[OSD([sQuery(id+"F6.wireOp",EDGE,"E28.bottom"),sQuery(id+"F6.wireOp",EDGE,"E28.right")])]})});
            fillet(context, id + "F10", {"entities" : qUnion([Q0, Q1, Q2, Q3, Q4, Q5, Q6, Q7, Q8, Q9, Q10, Q11, Q12, Q13, Q14, Q15, Q16, Q17, Q18, Q19, Q20, Q21, Q22, Q23, Q24, Q25, Q26, Q27, Q28, Q29, Q30, Q31, Q32, Q33, Q34, Q35, Q36, Q37, Q38, Q39, Q40, Q41, Q42, Q43, Q44, Q45]), "tangentPropagation" : true, "radius" : 1 * mm, "defaultsChanged" : false, "vertexSettings" : [], "allowEdgeOverflow" : false});
        }
    });
